AUTODESK INVENTOR PART (.ipt)
format: ipt  version: 2015 (Build 190159000, 159)  size: 897,536 bytes
history: native  units: mm
features: other x19, loft x3, pattern_circular x3, sketch x1
ambient origin geometry x6: Origin, XZ Plane, X Axis, Y Axis, Z Axis, Center Point
bodies: Solid1 (feature_tree), 实体草图 (feature_tree)
feature tree (26):
  other  "网格平面 2"
  other  "齿实体"
  other  "齿平面"
  other  "起始草图"
  loft  "Loft"
  pattern_circular  "Circular Pattern"  [2 undecoded]
  other  "三维草图 (右)"
  other  "终止平面 (右)"
  loft  "放样 (右)"
  pattern_circular  "环形阵列 (右)"  [2 undecoded]
  other  "三维草图 (左)"
  other  "终止平面 (左)"
  loft  "放样 (左)"
  pattern_circular  "环形阵列 (左)"  [2 undecoded]
  other  "固定实体"
  other  "网格平面"
  other  "上平面"
  other  "齿实体草图"
  other  "终止平面"
  other  "终止草图"
  other  "Helical Curve Left"
  other  "终止草图 (左)"
  sketch  "Sketch6"  dims[d0=180.0mm d1=177.72316mm d2=181.897367mm d3=37.9mm d4=27.15395mm d5=90.0deg d7=98.388237mm d8=95.024967mm d9=251.465119mm d11=38.23mm d12=58.838175mm d15=56.82687mm d16=150.381276mm d17=0.0mm d18=90.0deg d19=0.0mm d20=90.0deg d21=600.0mm d22=360.0deg d26=393.171382mm d27=12.089387mm d28=180.0mm d29=-12.490458mm d30=58.838175mm d31=56.82687mm d32=150.381276mm d35=0.0mm d37=0.0mm d39=0.0mm d40=90.0deg d41=600.0mm d42=360.0deg d46=90.0deg d47=90.0deg d48=0.0mm d49=0.0mm d50=90.0deg d51=0.523599mm d52=0.0mm d53=0.0mm d54=0.0mm d56=17.373125mm d57=289.584989mm d58=280.212989mm d59=173.177736mm d60=167.573089mm d61=173.177736mm d62=167.573089mm d65=393.171382mm d66=31.5mm d67=180.0mm d68=-12.490458mm d69=12.089387mm d70=56.82687mm d71=150.381276mm d72=58.838175mm d73=167.573089mm d74=173.177736mm d75=0.0mm d77=0.0mm d79=0.0mm d80=90.0deg d81=600.0mm d82=360.0deg d84=10.0mm d85=20.0mm d86=20.0mm d87=10.0mm d88=0.0mm d89=0.0mm d90=90.0deg d91=90.0deg d92=90.0deg d93=90.0deg]
  other  "Srf1"
  other  "Helical Curve Right"
  other  "终止草图 (右)"
note: 6 required parameter values undecoded (feature->parameter linkage not recoverable at this tier; creation-order binding heuristic only, values carry confidence <= 0.55)
